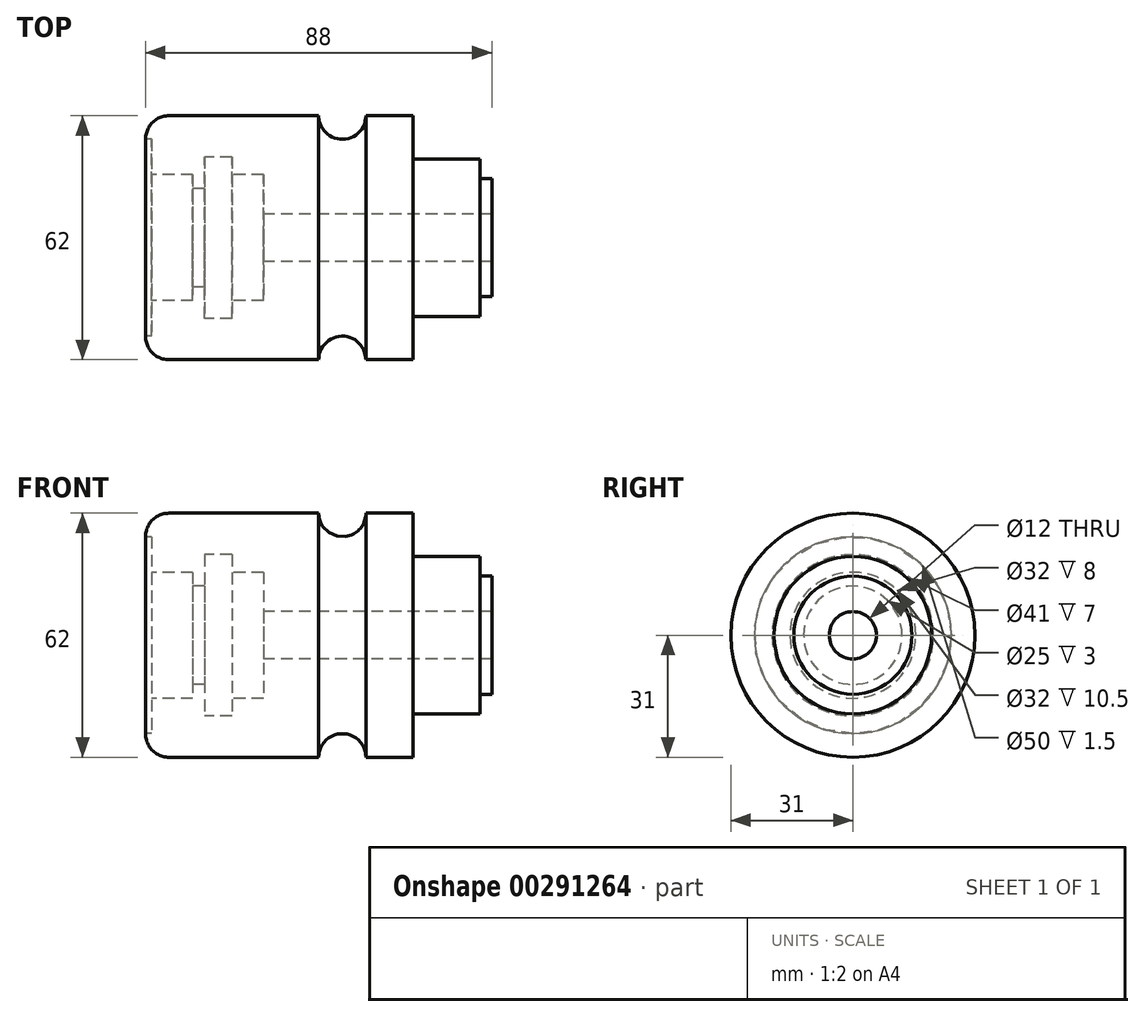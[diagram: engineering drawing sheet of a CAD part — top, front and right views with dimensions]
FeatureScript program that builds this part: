
annotation { "Feature Type Name" : "Feature", "Feature Type Description" : "" }
export const myFeature = defineFeature(function(context is Context, id is Id, definition is map)
    precondition{}
    {
        {
            var Q0;
            Q0=qCreatedBy(makeId("Front.planeOp"),FACE);
            var sketch = newSketch(context, id + "F0", { "sketchPlane" : qUnion([Q0])});
            skLineSegment(sketch, "E0", {"start": v(0, 0) * mm, "end": v(205.64, 0) * mm, "construction": true});
            skLineSegment(sketch, "E1", {"start": v(0, 0) * mm, "end": v(0, 31) * mm});
            skLineSegment(sketch, "E2", {"start": v(0, 31) * mm, "end": v(44, 31) * mm});
            skLineSegment(sketch, "E3", {"start": v(68, 31) * mm, "end": v(68, 20) * mm});
            skLineSegment(sketch, "E4", {"start": v(68, 20) * mm, "end": v(85, 20) * mm});
            skLineSegment(sketch, "E5", {"start": v(85, 20) * mm, "end": v(85, 15) * mm});
            skLineSegment(sketch, "E6", {"start": v(85, 15) * mm, "end": v(88, 15) * mm});
            skLineSegment(sketch, "E7", {"start": v(88, 15) * mm, "end": v(88, 0) * mm});
            skLineSegment(sketch, "E8", {"start": v(88, 0) * mm, "end": v(0, 0) * mm});
            skArc(sketch, "E9", {"start": v(44, 31) * mm, "mid": v(50, 25) * mm, "end": v(56, 31) * mm});
            skLineSegment(sketch, "E10.trimOffspring", {"start": v(56, 31) * mm, "end": v(68, 31) * mm});
            skSolve(sketch);
        }
        {
            var Q0;
            Q0 = qSketchRegion(id + "F0", true);
            var Q1;
            Q1=sQuery(id+"F0.wireOp",EDGE,"E8");
            revolve(context, id + "F1", {"entities" : qUnion([Q0]), "axis" : qUnion([Q1]), "revolveType" : RevolveType.FULL});
        }
        {
            var Q0;
            Q0=qCreatedBy(makeId("Front.planeOp"),FACE);
            var sketch = newSketch(context, id + "F2", { "sketchPlane" : qUnion([Q0])});
            skLineSegment(sketch, "E11", {"start": v(0, 25) * mm, "end": v(1.5, 25) * mm});
            skLineSegment(sketch, "E12", {"start": v(1.5, 25) * mm, "end": v(1.5, 16) * mm});
            skLineSegment(sketch, "E13", {"start": v(1.5, 16) * mm, "end": v(12, 16) * mm});
            skLineSegment(sketch, "E14", {"start": v(12, 16) * mm, "end": v(12, 12.5) * mm});
            skLineSegment(sketch, "E15", {"start": v(12, 12.5) * mm, "end": v(15, 12.5) * mm});
            skLineSegment(sketch, "E16", {"start": v(15, 12.5) * mm, "end": v(15, 20.5) * mm});
            skLineSegment(sketch, "E17", {"start": v(15, 20.5) * mm, "end": v(22, 20.5) * mm});
            skLineSegment(sketch, "E18", {"start": v(22, 20.5) * mm, "end": v(22, 16) * mm});
            skLineSegment(sketch, "E19", {"start": v(30, 16) * mm, "end": v(30, 6) * mm});
            skLineSegment(sketch, "E20", {"start": v(30, 6) * mm, "end": v(88, 6) * mm});
            skLineSegment(sketch, "E21", {"start": v(88, 6) * mm, "end": v(88, 0) * mm});
            skLineSegment(sketch, "E22", {"start": v(88, 0) * mm, "end": v(0, 0) * mm});
            skLineSegment(sketch, "E23", {"start": v(0, 0) * mm, "end": v(-22.96, 0) * mm, "construction": true});
            skLineSegment(sketch, "E24", {"start": v(0, 25) * mm, "end": v(0, 0) * mm});
            skLineSegment(sketch, "E25", {"start": v(22, 16) * mm, "end": v(30, 16) * mm});
            skSolve(sketch);
        }
        {
            var Q0;
            Q0 = qSketchRegion(id + "F2", true);
            var Q1;
            Q1=sQuery(id+"F2.wireOp",EDGE,"E23");
            revolve(context, id + "F3", {"operationType" : NewBodyOperationType.REMOVE, "entities" : qUnion([Q0]), "axis" : qUnion([Q1]), "revolveType" : RevolveType.FULL, "oppositeDirection" : true});
        }
        {
            var Q0;
            Q0=makeQuery(id+"F1.opRevolve","SWEPT_EDGE",EDGE,{"disambiguationData":[OSD([sQuery(id+"F0.wireOp",EDGE,"E1"),sQuery(id+"F0.wireOp",EDGE,"E2")])]});
            fillet(context, id + "F4", {"entities" : qUnion([Q0]), "radius" : 6 * mm, "tangentPropagation" : true, "allowEdgeOverflow" : false});
        }
    });
